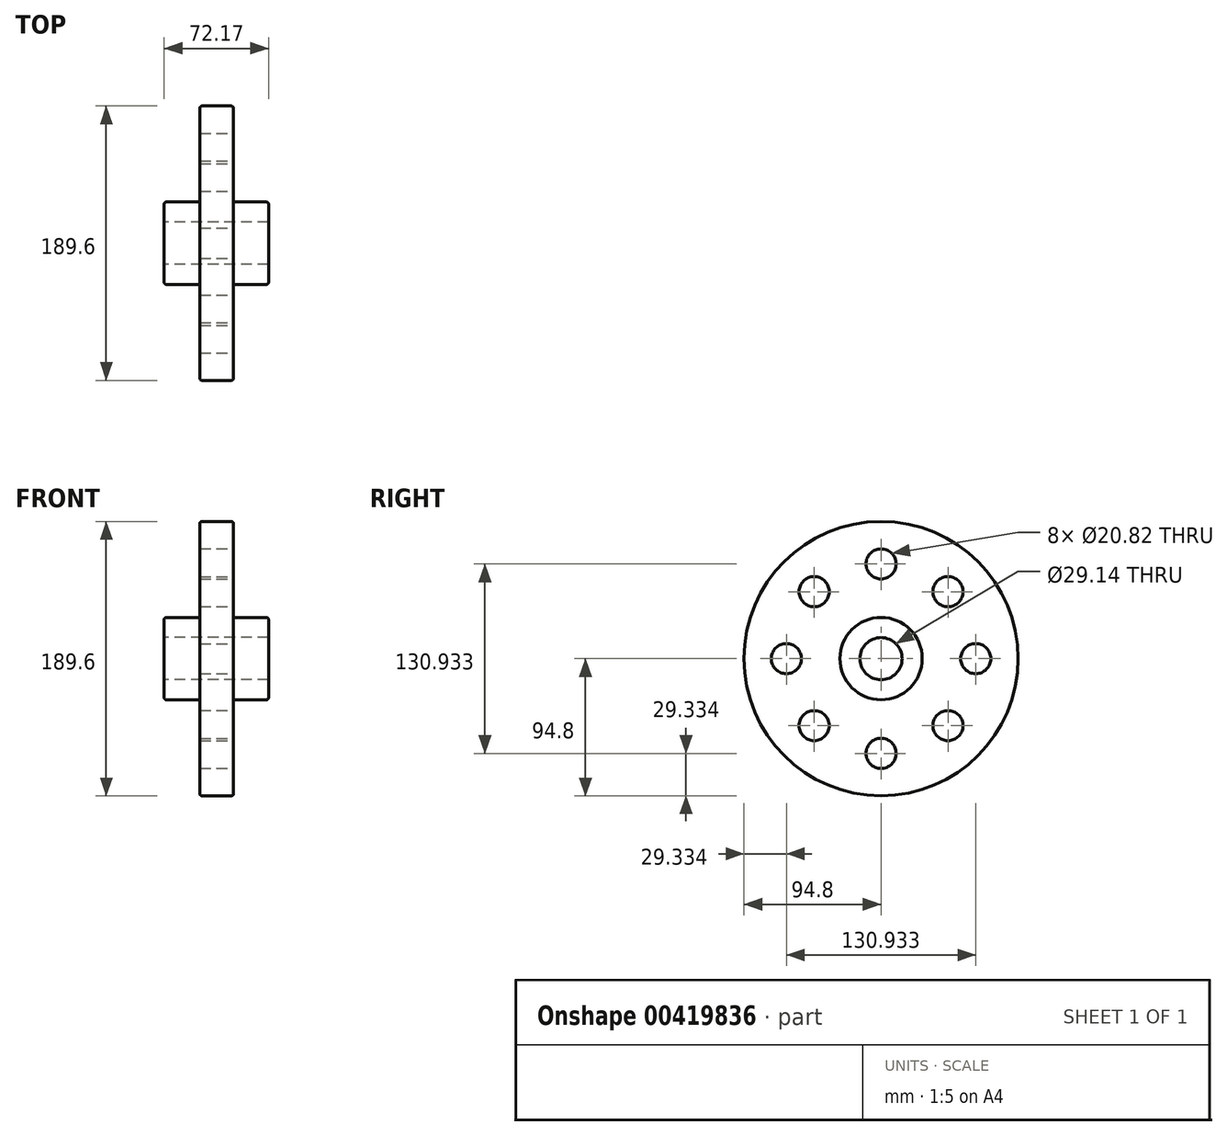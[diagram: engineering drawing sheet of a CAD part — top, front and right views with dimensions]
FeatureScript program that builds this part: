
annotation { "Feature Type Name" : "Feature", "Feature Type Description" : "" }
export const myFeature = defineFeature(function(context is Context, id is Id, definition is map)
    precondition{}
    {
        {
            var Q0;
            Q0=qCreatedBy(makeId("Front.planeOp"),FACE);
            var sketch = newSketch(context, id + "F0", { "sketchPlane" : qUnion([Q0])});
            skLineSegment(sketch, "E0", {"start": v(-168.1, 0) * mm, "end": v(117.89, 0) * mm, "construction": true});
            skLineSegment(sketch, "E1", {"start": v(-35.41, 14.57) * mm, "end": v(36.76, 14.57) * mm});
            skLineSegment(sketch, "E2", {"start": v(36.76, 14.57) * mm, "end": v(36.76, 28.46) * mm});
            skLineSegment(sketch, "E3", {"start": v(36.76, 28.46) * mm, "end": v(12.55, 28.46) * mm});
            skLineSegment(sketch, "E4", {"start": v(12.55, 28.46) * mm, "end": v(12.55, 94.8) * mm});
            skLineSegment(sketch, "E5", {"start": v(12.55, 94.8) * mm, "end": v(-10.76, 94.8) * mm});
            skLineSegment(sketch, "E6", {"start": v(-10.76, 94.8) * mm, "end": v(-10.76, 28.46) * mm});
            skLineSegment(sketch, "E7", {"start": v(-10.76, 28.46) * mm, "end": v(-35.41, 28.46) * mm});
            skLineSegment(sketch, "E8", {"start": v(-35.41, 28.46) * mm, "end": v(-35.41, 14.57) * mm});
            skSolve(sketch);
        }
        {
            var Q0;
            Q0 = qSketchRegion(id + "F0", true);
            var Q1;
            Q1=sQuery(id+"F0.wireOp",EDGE,"E0");
            revolve(context, id + "F1", {"entities" : qUnion([Q0]), "axis" : qUnion([Q1]), "revolveType" : RevolveType.FULL});
        }
        {
            var Q0;
            Q0=makeQuery(id+"F1.opRevolve","SWEPT_FACE",FACE,{"disambiguationData":[OSD([sQuery(id+"F0.wireOp",EDGE,"E4")])]});
            var sketch = newSketch(context, id + "F2", { "sketchPlane" : qUnion([Q0])});
            skCircle(sketch, "E9", {"center": v(0, 0) * mm, "radius": 65.47 * mm, "construction": true});
            skCircle(sketch, "E10", {"center": v(0, 65.47) * mm, "radius": 10.41 * mm});
            skCircle(sketch, "E11.1.0", {"center": v(-46.3, 46.3) * mm, "radius": 10.41 * mm});
            skCircle(sketch, "E11.2.0", {"center": v(-65.47, 0) * mm, "radius": 10.41 * mm});
            skCircle(sketch, "E11.3.0", {"center": v(-46.3, -46.3) * mm, "radius": 10.41 * mm});
            skCircle(sketch, "E11.4.0", {"center": v(0, -65.47) * mm, "radius": 10.41 * mm});
            skCircle(sketch, "E11.5.0", {"center": v(46.3, -46.3) * mm, "radius": 10.41 * mm});
            skCircle(sketch, "E11.6.0", {"center": v(65.47, 0) * mm, "radius": 10.41 * mm});
            skCircle(sketch, "E11.7.0", {"center": v(46.3, 46.3) * mm, "radius": 10.41 * mm});
            skSolve(sketch);
        }
        {
            var Q0;
            Q0 = qSketchRegion(id + "F2", true);
            var Q1;
            Q1=makeQuery(id+"F2.imprint","IMPRINT",FACE,{"disambiguationData":[TD([[makeQuery(id+"F2.imprint","IMPRINT",EDGE,{"derivedFrom":sQuery(id+"F2.wireOp",EDGE,"E10")}),1.0]])]});
            extrude(context, id + "F3", {"entities" : qUnion([Q0, Q1]), "operationType" : NewBodyOperationType.REMOVE, "endBound" : BoundingType.THROUGH_ALL, "oppositeDirection" : true, "depth" : 25.4 * mm});
        }
        {
            var Q0;
            Q0=makeQuery(id+"F1.opRevolve","SWEPT_EDGE",EDGE,{"disambiguationData":[OSD([sQuery(id+"F0.wireOp",EDGE,"E5"),sQuery(id+"F0.wireOp",EDGE,"E6")])]});
            fillet(context, id + "F4", {"entities" : qUnion([Q0]), "radius" : 1.52 * mm, "tangentPropagation" : true, "allowEdgeOverflow" : false});
        }
        {
            var Q0;
            Q0=makeQuery(id+"F1.opRevolve","SWEPT_EDGE",EDGE,{"disambiguationData":[OSD([sQuery(id+"F0.wireOp",EDGE,"E4"),sQuery(id+"F0.wireOp",EDGE,"E5")])]});
            var Q1;
            Q1=makeQuery(id+"F1.opRevolve","SWEPT_EDGE",EDGE,{"disambiguationData":[OSD([sQuery(id+"F0.wireOp",EDGE,"E2"),sQuery(id+"F0.wireOp",EDGE,"E3")])]});
            var Q2;
            Q2=makeQuery(id+"F1.opRevolve","SWEPT_EDGE",EDGE,{"disambiguationData":[OSD([sQuery(id+"F0.wireOp",EDGE,"E7"),sQuery(id+"F0.wireOp",EDGE,"E8")])]});
            fillet(context, id + "F5", {"entities" : qUnion([Q0, Q1, Q2]), "radius" : 1.52 * mm, "tangentPropagation" : true, "allowEdgeOverflow" : false});
        }
    });
